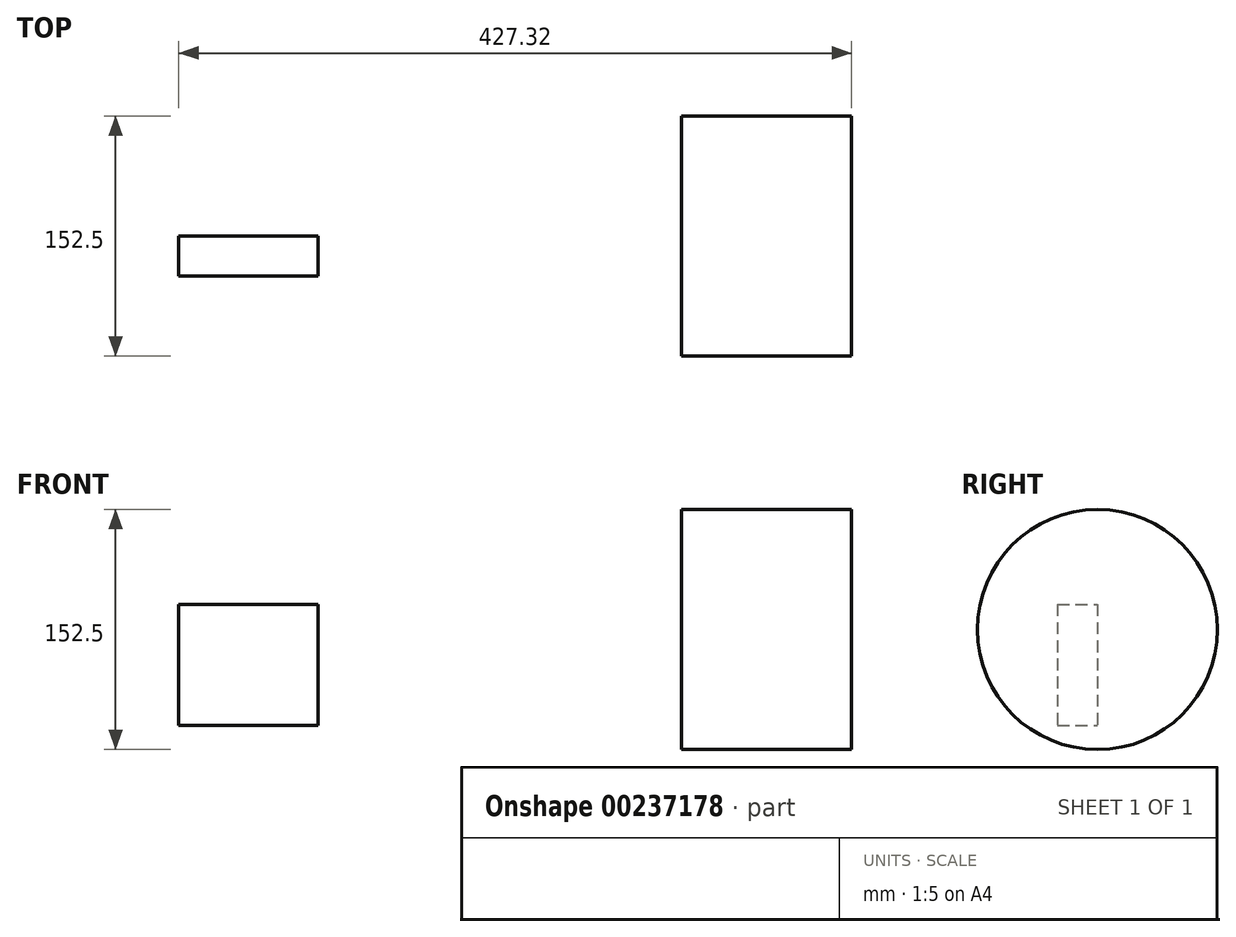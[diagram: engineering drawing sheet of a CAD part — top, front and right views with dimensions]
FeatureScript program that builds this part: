
annotation { "Feature Type Name" : "Feature", "Feature Type Description" : "" }
export const myFeature = defineFeature(function(context is Context, id is Id, definition is map)
    precondition{}
    {
        {
            var Q0;
            Q0=qCreatedBy(makeId("Right.planeOp"),FACE);
            var sketch = newSketch(context, id + "F0", { "sketchPlane" : qUnion([Q0])});
            skCircle(sketch, "E0", {"center": v(0, 0) * mm, "radius": 76.25 * mm});
            skSolve(sketch);
        }
        {
            var Q0;
            Q0=makeQuery(id+"F0.imprint","IMPRINT",FACE,{"disambiguationData":[TD([[makeQuery(id+"F0.imprint","IMPRINT",EDGE,{"derivedFrom":sQuery(id+"F0.wireOp",EDGE,"E0")}),1.0]])]});
            extrude(context, id + "F1", {"entities" : qUnion([Q0]), "depth" : 107.95 * mm});
        }
        {
            var Q0;
            Q0=qCreatedBy(makeId("Front.planeOp"),FACE);
            var sketch = newSketch(context, id + "F2", { "sketchPlane" : qUnion([Q0])});
            skLineSegment(sketch, "E1.bottom", {"start": v(-319.37, 16.1) * mm, "end": v(-230.93, 16.1) * mm});
            skLineSegment(sketch, "E1.top", {"start": v(-319.37, -61) * mm, "end": v(-230.93, -61) * mm});
            skLineSegment(sketch, "E1.left", {"start": v(-319.37, 16.1) * mm, "end": v(-319.37, -61) * mm});
            skLineSegment(sketch, "E1.right", {"start": v(-230.93, 16.1) * mm, "end": v(-230.93, -61) * mm});
            skLineSegment(sketch, "E2.bottom", {"start": v(-230.93, 16.1) * mm, "end": v(-230.93, 16.1) * mm});
            skLineSegment(sketch, "E2.top", {"start": v(-230.93, -8.2) * mm, "end": v(-230.93, -8.2) * mm});
            skLineSegment(sketch, "E2.left", {"start": v(-230.93, 16.1) * mm, "end": v(-230.93, -8.2) * mm});
            skLineSegment(sketch, "E2.right", {"start": v(-230.93, 16.1) * mm, "end": v(-230.93, -8.2) * mm});
            skSolve(sketch);
        }
        {
            var Q0;
            Q0=makeQuery(id+"F2.imprint","IMPRINT",FACE,{"disambiguationData":[TD([[makeQuery(id+"F2.imprint","IMPRINT",EDGE,{"derivedFrom":sQuery(id+"F2.wireOp",EDGE,"E1.bottom")}),-1.0]])]});
            extrude(context, id + "F3", {"entities" : qUnion([Q0]), "depth" : 25.4 * mm});
        }
    });
